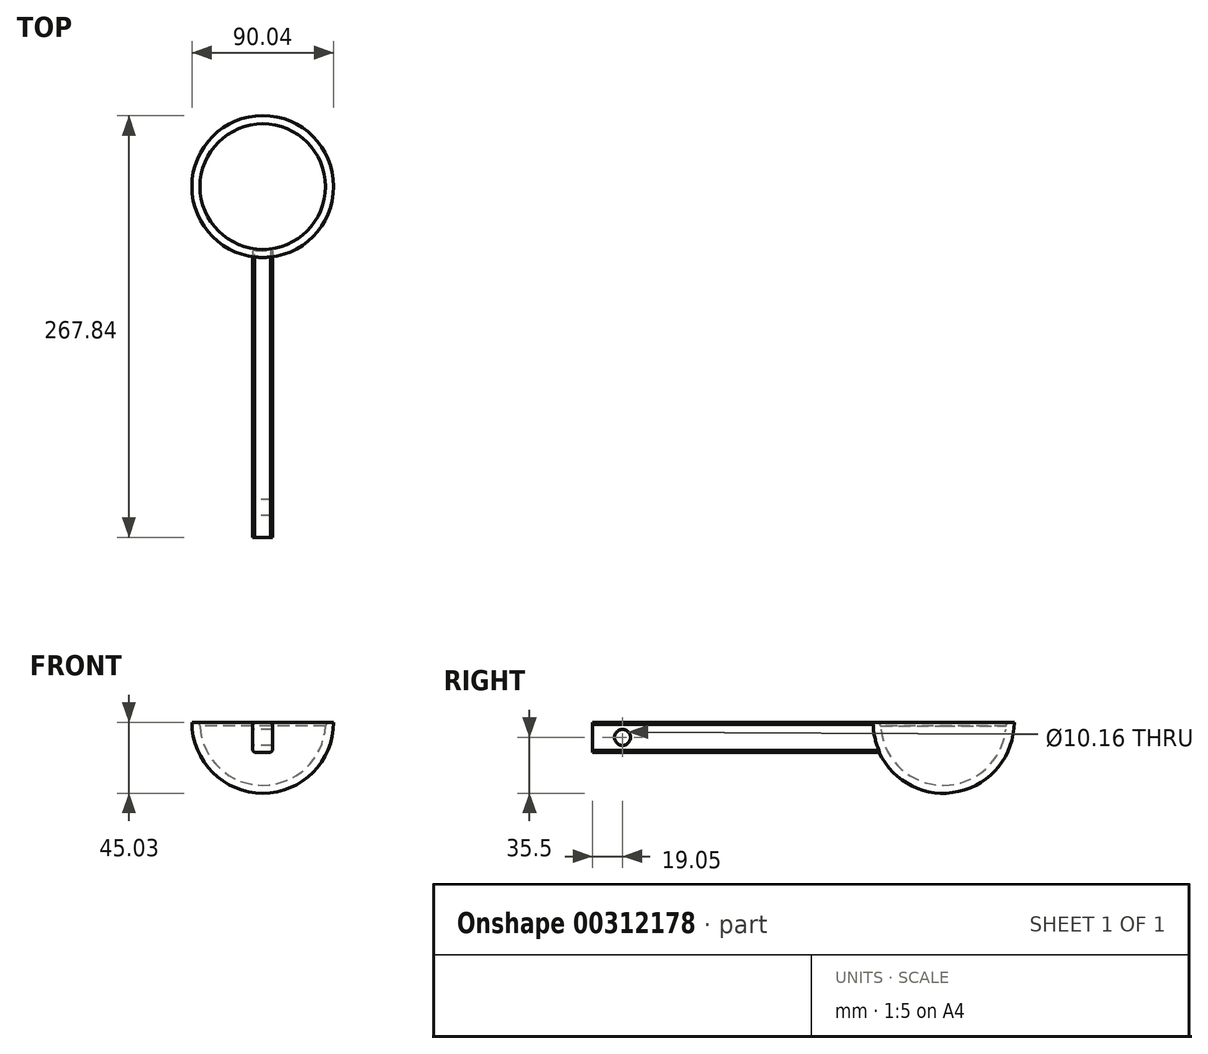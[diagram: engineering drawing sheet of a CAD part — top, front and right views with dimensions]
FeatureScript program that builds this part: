
annotation { "Feature Type Name" : "Feature", "Feature Type Description" : "" }
export const myFeature = defineFeature(function(context is Context, id is Id, definition is map)
    precondition{}
    {
        {
            var Q0;
            Q0=qCreatedBy(makeId("Right.planeOp"),FACE);
            var sketch = newSketch(context, id + "F0", { "sketchPlane" : qUnion([Q0])});
            skLineSegment(sketch, "E0.bottom", {"start": v(76.2, 9.53) * mm, "end": v(-76.2, 9.53) * mm});
            skLineSegment(sketch, "E0.right", {"start": v(-76.2, 9.53) * mm, "end": v(-76.2, -9.53) * mm});
            skPoint(sketch, "E0.middle", {"position": v(0, 0) * mm});
            skLineSegment(sketch, "E1", {"start": v(76.2, 9.53) * mm, "end": v(166.24, 9.53) * mm});
            skArc(sketch, "E2.MirrorCS", {"start": v(166.24, 9.53) * mm, "mid": v(121.22, -35.5) * mm, "end": v(76.2, 9.53) * mm});
            skLineSegment(sketch, "E3", {"start": v(-76.2, -9.53) * mm, "end": v(80.43, -9.53) * mm});
            skSolve(sketch);
        }
        {
            var Q0;
            {var subQ0=sQuery(id+"F0.wireOp",EDGE,"E0.bottom");Q0=makeQuery(id+"F0.imprint","IMPRINT",FACE,{"disambiguationData":[TD([[makeQuery(id+"F0.imprint","IMPRINT",EDGE,{"derivedFrom":subQ0}),1.0]])]});}
            extrude(context, id + "F1", {"entities" : qUnion([Q0]), "endBound" : BoundingType.SYMMETRIC, "depth" : 12.7 * mm});
        }
        {
            var Q0;
            {var subQ0=sQuery(id+"F0.wireOp",EDGE,"E1");Q0=makeQuery(id+"F0.imprint","IMPRINT",FACE,{"disambiguationData":[TD([[makeQuery(id+"F0.imprint","IMPRINT",EDGE,{"derivedFrom":subQ0}),-1.0]])]});}
            var Q1;
            Q1=sQuery(id+"F0.wireOp",EDGE,"E1");
            revolve(context, id + "F2", {"entities" : qUnion([Q0]), "axis" : qUnion([Q1]), "revolveType" : RevolveType.FULL});
        }
        {
            var Q0;
            Q0=makeQuery(id+"F1.opExtrude","SWEPT_FACE",FACE,{"disambiguationData":[OSD([sQuery(id+"F0.wireOp",EDGE,"E0.right")])]});
            extrude(context, id + "F3", {"entities" : qUnion([Q0]), "operationType" : NewBodyOperationType.ADD, "depth" : 25.4 * mm});
        }
        {
            var Q0;
            Q0=makeQuery(id+"F3.opExtrude","CAP_FACE",FACE,{"disambiguationData":[OSD([sQuery(id+"F0.wireOp",EDGE,"E0.right")])],"isStart":false});
            var sketch = newSketch(context, id + "F4", { "sketchPlane" : qUnion([Q0])});
            skLineSegment(sketch, "E4.0.0", {"start": v(-6.35, 9.53) * mm, "end": v(-6.35, -9.52) * mm});
            skLineSegment(sketch, "E4.0.1", {"start": v(-6.35, -9.52) * mm, "end": v(6.35, -9.52) * mm});
            skLineSegment(sketch, "E4.0.2", {"start": v(6.35, -9.52) * mm, "end": v(6.35, 9.53) * mm});
            skLineSegment(sketch, "E4.0.3", {"start": v(6.35, 9.53) * mm, "end": v(-6.35, 9.53) * mm});
            skLineSegment(sketch, "E5", {"start": v(64.15, 9.53) * mm, "end": v(-69.29, 9.53) * mm});
            skLineSegment(sketch, "E6", {"start": v(-69.29, 9.53) * mm, "end": v(-69.29, 62.6) * mm});
            skLineSegment(sketch, "E7", {"start": v(-69.29, 62.6) * mm, "end": v(64.15, 62.6) * mm});
            skLineSegment(sketch, "E8", {"start": v(64.15, 62.6) * mm, "end": v(64.15, 9.53) * mm});
            skSolve(sketch);
        }
        {
            var Q0;
            {var subQ0=sQuery(id+"F4.wireOp",EDGE,"E6");Q0=makeQuery(id+"F4.imprint","IMPRINT",FACE,{"disambiguationData":[TD([[makeQuery(id+"F4.imprint","IMPRINT",EDGE,{"derivedFrom":subQ0}),-1.0]])]});}
            extrude(context, id + "F5", {"entities" : qUnion([Q0]), "operationType" : NewBodyOperationType.REMOVE, "endBound" : BoundingType.THROUGH_ALL, "oppositeDirection" : true, "depth" : 25.4 * mm});
        }
        {
            var Q0;
            Q0=makeQuery(id+"F5.boolean.opBoolean","COPY",FACE,{"derivedFrom":makeQuery(id+"F5.opExtrude","SWEPT_FACE",FACE,{"disambiguationData":[OSD([sQuery(id+"F4.wireOp",EDGE,"E5")])]})});
            shell(context, id + "F6", {"entities" : qUnion([Q0]), "thickness" : 5.08 * mm});
        }
        {
            var Q0;
            Q0=qCreatedBy(makeId("Front.planeOp"),FACE);
            cPlane(context, id + "F7", {"entities" : qUnion([Q0]), "cplaneType" : CPlaneType.OFFSET, "offset" : 101.6 * mm, "width" : 152.4 * mm, "height" : 152.4 * mm});
        }
        {
            var Q0;
            Q0=qCreatedBy(id+"F7.planeOp",FACE);
            var sketch = newSketch(context, id + "F8", { "sketchPlane" : qUnion([Q0])});
            skLineSegment(sketch, "E9.0", {"start": v(-6.35, 9.53) * mm, "end": v(-6.35, -9.53) * mm});
            skLineSegment(sketch, "E10.0", {"start": v(6.35, 9.53) * mm, "end": v(6.35, -9.53) * mm});
            skLineSegment(sketch, "E11.0", {"start": v(6.35, 9.53) * mm, "end": v(-6.35, 9.53) * mm});
            skLineSegment(sketch, "E12.0", {"start": v(6.35, -9.53) * mm, "end": v(-6.35, -9.53) * mm});
            skSolve(sketch);
        }
        {
            var Q0;
            Q0 = qSketchRegion(id + "F8", true);
            var Q1;
            Q1=makeQuery(id+"F2.opRevolve","SWEPT_FACE",FACE,{"disambiguationData":[OSD([sQuery(id+"F0.wireOp",EDGE,"E2.MirrorCS")])]});
            extrude(context, id + "F9", {"entities" : qUnion([Q0]), "endBound" : BoundingType.UP_TO_SURFACE, "oppositeDirection" : true, "endBoundEntityFace" : qUnion([Q1]), "depth" : 25.4 * mm});
        }
        {
            var Q0;
            Q0=makeQuery(id+"F1.opExtrude","SWEPT_BODY",BODY,{"disambiguationData":[OSD([sQuery(id+"F0.wireOp",EDGE,"E0.bottom"),sQuery(id+"F0.wireOp",EDGE,"E0.right"),sQuery(id+"F0.wireOp",EDGE,"E2.MirrorCS"),sQuery(id+"F0.wireOp",EDGE,"E3")])]});
            deleteBodies(context, id + "F10", {"entities" : qUnion([Q0])});
        }
        {
            var Q0;
            Q0=makeQuery(id+"F6.opShell","OFFSET_EDGE",EDGE,{"disambiguationData":[OSD([sQuery(id+"F0.wireOp",EDGE,"E2.MirrorCS"),sQuery(id+"F4.wireOp",EDGE,"E5")])]});
            fillet(context, id + "F11", {"entities" : qUnion([Q0]), "radius" : 2.54 * mm, "tangentPropagation" : true, "allowEdgeOverflow" : false});
        }
        {
            var Q0;
            Q0=makeQuery(id+"F9.opExtrude","SWEPT_EDGE",EDGE,{"disambiguationData":[OSD([sQuery(id+"F8.wireOp",EDGE,"E9.0"),sQuery(id+"F8.wireOp",EDGE,"E11.0")])]});
            var Q1;
            Q1=makeQuery(id+"F9.opExtrude","SWEPT_EDGE",EDGE,{"disambiguationData":[OSD([sQuery(id+"F8.wireOp",EDGE,"E10.0"),sQuery(id+"F8.wireOp",EDGE,"E11.0")])]});
            var Q2;
            Q2=makeQuery(id+"F9.opExtrude","SWEPT_EDGE",EDGE,{"disambiguationData":[OSD([sQuery(id+"F8.wireOp",EDGE,"E9.0"),sQuery(id+"F8.wireOp",EDGE,"E12.0")])]});
            var Q3;
            Q3=makeQuery(id+"F9.opExtrude","SWEPT_EDGE",EDGE,{"disambiguationData":[OSD([sQuery(id+"F8.wireOp",EDGE,"E10.0"),sQuery(id+"F8.wireOp",EDGE,"E12.0")])]});
            chamfer(context, id + "F12", {"entities" : qUnion([Q0, Q1, Q2, Q3]), "width" : 1.27 * mm, "tangentPropagation" : true});
        }
        {
            var Q0;
            Q0=makeQuery(id+"F9.opExtrude","SWEPT_FACE",FACE,{"disambiguationData":[OSD([sQuery(id+"F8.wireOp",EDGE,"E9.0")])]});
            var sketch = newSketch(context, id + "F13", { "sketchPlane" : qUnion([Q0])});
            skCircle(sketch, "E13", {"center": v(82.55, 0) * mm, "radius": 5.08 * mm});
            skSolve(sketch);
        }
        {
            var Q0;
            Q0 = qSketchRegion(id + "F13", true);
            extrude(context, id + "F14", {"entities" : qUnion([Q0]), "operationType" : NewBodyOperationType.REMOVE, "oppositeDirection" : true, "depth" : 25.4 * mm});
        }
    });
